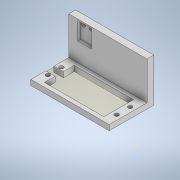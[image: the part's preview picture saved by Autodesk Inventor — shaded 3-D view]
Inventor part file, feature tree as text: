
AUTODESK INVENTOR PART (.ipt)
format: ipt  version: 2021 (Build 250183000, 183)  size: 193,024 bytes
history: native  units: mm
features: sketch x5, extrude x4, other x1, plane x1
ambient origin geometry x8: Origin, YZ Plane, XZ Plane, XY Plane, X Axis, Y Axis, Z Axis, Center Point
bodies: Body1 (feature_tree)
feature tree (11):
  other  "Sólido1"
  plane  "Plano de trabajo1"
  extrude  "Extrusión2"  Depth=5.0mm
  sketch  "Boceto3"  dims[d10=7.0mm d11=2.0mm]
  extrude  "Extrusión3"  Depth=2.0mm
  extrude  "Extrusión4"  Depth=3.0mm
  extrude  "Extrusión5"  Depth=7.0mm
  sketch  "Boceto2"  dims[d8=5.0mm d9=5.0mm]
  sketch  "Boceto4"  dims[d12=3.0mm d13=3.0mm]
  sketch  "Boceto5"  dims[d14=1.0mm d15=7.0mm]
  sketch  "Boceto6"  dims[d16=1.0mm d17=1.0mm d18=4.0mm d19=4.0mm d20=4.0mm d21=0.0mm d22=3.0mm d23=3.0mm d24=14.1mm d25=4.0mm d26=14.0mm d27=10.5mm d28=10.1mm d29=23.0mm d30=10.0mm d31=0.1mm d32=0.1mm d33=13.0mm d34=10.1mm d35=2.0mm d36=2.0mm d38=0.05mm d39=3.0mm d40=6.0mm d41=3.0mm d42=5.0mm d43=0.0mm d44=10.5mm d45=2.05mm d46=3.0mm d47=6.0mm d48=3.0mm d49=3.0mm d50=0.0mm d51=4.0mm d52=0.0mm]
